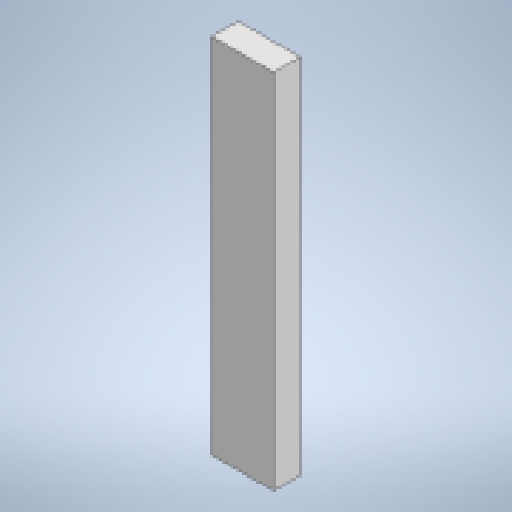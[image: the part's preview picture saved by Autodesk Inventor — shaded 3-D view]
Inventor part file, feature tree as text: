
AUTODESK INVENTOR PART (.ipt)
format: ipt  version: 2025.1 (Build 291241020, 241B)  size: 130,048 bytes
history: native  units: in
note: dims shown in document units (in); Inventor stores cm internally (conversion verified against a paired STEP export)
features: other x4, reference x3, extrude x1, sketch x1
ambient origin geometry x8: Origin, YZ Plane, XZ Plane, XY Plane, X Axis, Y Axis, Z Axis, Center Point
bodies: Solid1 (feature_tree)
feature tree (9):
  extrude  "Extrusion1"  Depth=1.5in TaperAngle=0.0deg
  sketch  "Sketch1"  dims[d0=3.5in d1=1.5in d2=0.0in]
  reference  "Reference1"
  reference  "Reference2"
  reference  "Reference3"
  other  "<userpath>\Documents\Tburn24\F_Legs2\F_Legs2.iam"
  other  "F_Legs2.iam"
  other  "side-side1:1"
  other  "8'x2x4:4"
